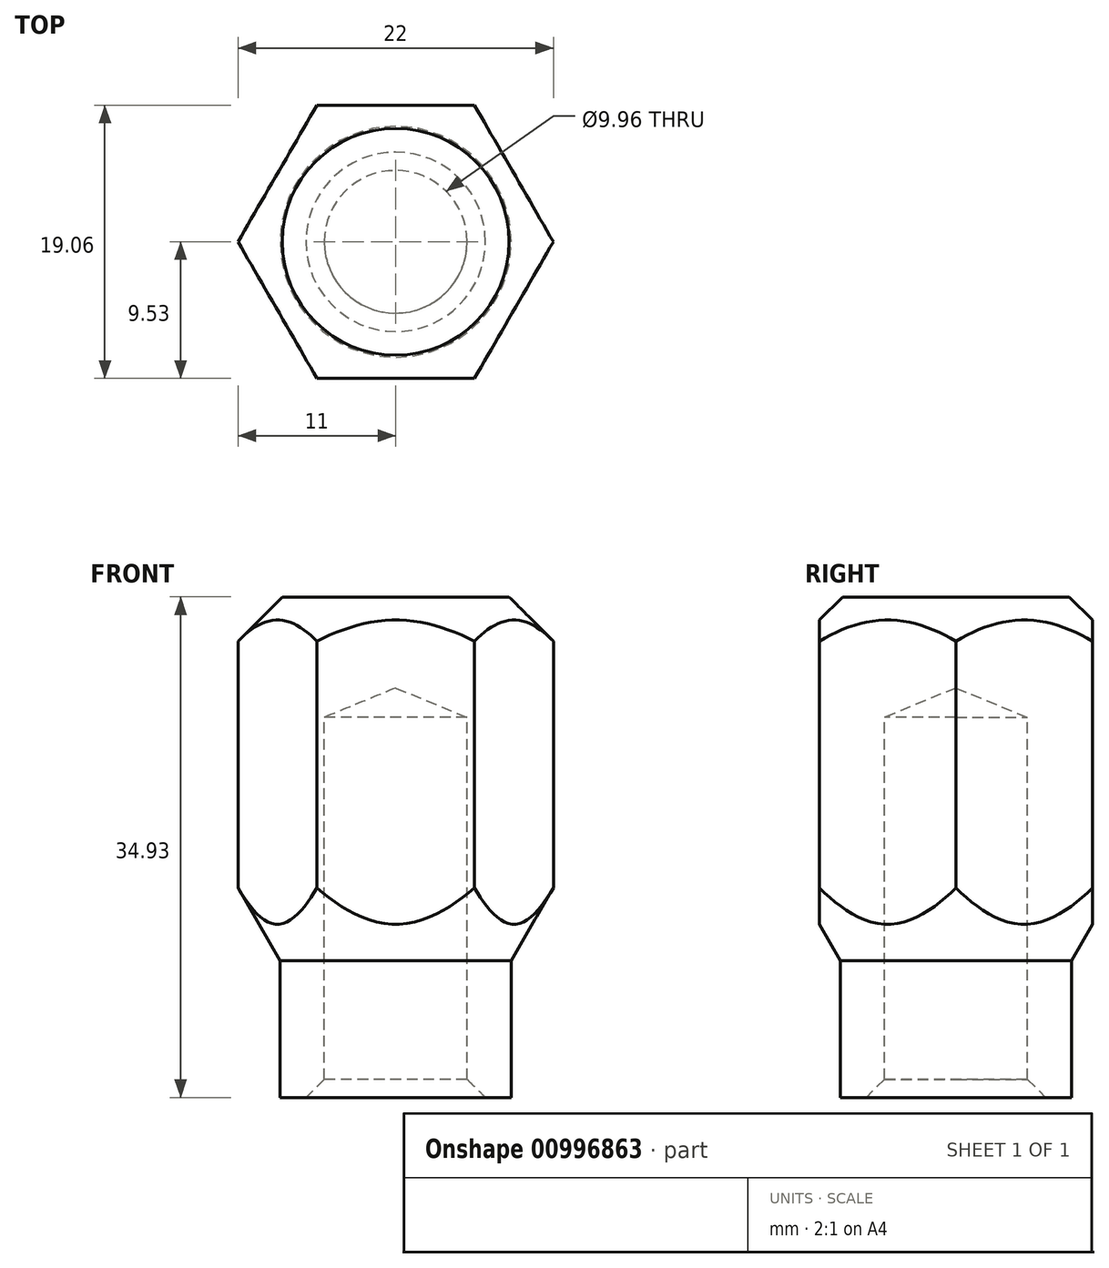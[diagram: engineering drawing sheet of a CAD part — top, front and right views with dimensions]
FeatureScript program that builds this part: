
annotation { "Feature Type Name" : "Feature", "Feature Type Description" : "" }
export const myFeature = defineFeature(function(context is Context, id is Id, definition is map)
    precondition{}
    {
        {
            var Q0;
            Q0=qCreatedBy(makeId("Front.planeOp"),FACE);
            var sketch = newSketch(context, id + "F0", { "sketchPlane" : qUnion([Q0])});
            skLineSegment(sketch, "E0", {"start": v(0, 0) * mm, "end": v(4.98, 0) * mm});
            skLineSegment(sketch, "E1", {"start": v(8.05, 0) * mm, "end": v(8.05, 9.53) * mm});
            skLineSegment(sketch, "E2", {"start": v(8.05, 9.53) * mm, "end": v(12.7, 17.58) * mm});
            skLineSegment(sketch, "E3", {"start": v(0, 0) * mm, "end": v(0, 28.58) * mm});
            skLineSegment(sketch, "E4", {"start": v(0, 28.58) * mm, "end": v(4.98, 28.58) * mm, "construction": true});
            skLineSegment(sketch, "E5", {"start": v(4.98, 28.58) * mm, "end": v(4.98, 1.27) * mm});
            skLineSegment(sketch, "E6", {"start": v(0, 0) * mm, "end": v(0, -1.59) * mm});
            skLineSegment(sketch, "E7", {"start": v(0, 28.58) * mm, "end": v(4.98, 26.53) * mm});
            skLineSegment(sketch, "E8", {"start": v(4.98, 1.27) * mm, "end": v(6.26, 0) * mm});
            skPoint(sketch, "E9.orphan", {"position": v(4.98, 0) * mm});
            skLineSegment(sketch, "E10.trimOffspring", {"start": v(6.26, 0) * mm, "end": v(8.05, 0) * mm});
            skLineSegment(sketch, "E11", {"start": v(12.7, 17.58) * mm, "end": v(12.7, 31.75) * mm, "construction": true});
            skLineSegment(sketch, "E12", {"start": v(0, 28.58) * mm, "end": v(0, 34.93) * mm});
            skLineSegment(sketch, "E13", {"start": v(0, 34.93) * mm, "end": v(7.92, 34.93) * mm});
            skLineSegment(sketch, "E14", {"start": v(12.7, 34.93) * mm, "end": v(12.7, 17.58) * mm});
            skLineSegment(sketch, "E15", {"start": v(12.7, 31.75) * mm, "end": v(9.53, 34.93) * mm});
            skLineSegment(sketch, "E16", {"start": v(12.7, 34.93) * mm, "end": v(9.53, 34.93) * mm, "construction": true});
            skLineSegment(sketch, "E17", {"start": v(12.7, 34.93) * mm, "end": v(12.7, 30.15) * mm, "construction": true});
            skLineSegment(sketch, "E18", {"start": v(12.7, 30.15) * mm, "end": v(7.92, 34.93) * mm});
            skSolve(sketch);
        }
        {
            var Q0;
            Q0 = qSketchRegion(id + "F0", true);
            var Q1;
            Q1=sQuery(id+"F0.wireOp",EDGE,"E3");
            revolve(context, id + "F1", {"surfaceOperationType" : NewSurfaceOperationType.NEW, "entities" : qUnion([Q0]), "axis" : qUnion([Q1]), "revolveType" : RevolveType.FULL, "oppositeDirection" : true});
        }
        {
            var Q0;
            Q0=qCreatedBy(makeId("Top.planeOp"),FACE);
            var sketch = newSketch(context, id + "F2", { "sketchPlane" : qUnion([Q0])});
            skCircle(sketch, "E19", {"center": v(0, 0) * mm, "radius": 15.24 * mm});
            skLineSegment(sketch, "E20.bottom", {"start": v(9.53, -9.52) * mm, "end": v(-9.53, -9.53) * mm, "construction": true});
            skLineSegment(sketch, "E20.top", {"start": v(9.53, 9.53) * mm, "end": v(-9.53, 9.52) * mm, "construction": true});
            skLineSegment(sketch, "E20.left", {"start": v(9.53, -9.52) * mm, "end": v(9.53, 9.53) * mm, "construction": true});
            skLineSegment(sketch, "E20.right", {"start": v(-9.53, -9.53) * mm, "end": v(-9.53, 9.52) * mm, "construction": true});
            skCircle(sketch, "E21.cCircle", {"center": v(0, 0) * mm, "radius": 9.53 * mm, "construction": true});
            skLineSegment(sketch, "E21.0", {"start": v(5.5, -9.53) * mm, "end": v(-5.5, -9.53) * mm});
            skLineSegment(sketch, "E21.1", {"start": v(-5.5, -9.53) * mm, "end": v(-11, 0) * mm});
            skLineSegment(sketch, "E21.2", {"start": v(-11, 0) * mm, "end": v(-5.5, 9.52) * mm});
            skLineSegment(sketch, "E21.3", {"start": v(-5.5, 9.52) * mm, "end": v(5.5, 9.53) * mm});
            skLineSegment(sketch, "E21.4", {"start": v(5.5, 9.53) * mm, "end": v(11, 0) * mm});
            skLineSegment(sketch, "E21.5", {"start": v(11, 0) * mm, "end": v(5.5, -9.53) * mm});
            skPoint(sketch, "E21.0.midPoint", {"position": v(0, -9.53) * mm});
            skSolve(sketch);
        }
        {
            var Q0;
            Q0 = qSketchRegion(id + "F2", true);
            extrude(context, id + "F3", {"entities" : qUnion([Q0]), "operationType" : NewBodyOperationType.REMOVE, "depth" : 38.1 * mm, "offsetDistance" : 25.4 * mm});
        }
    });
